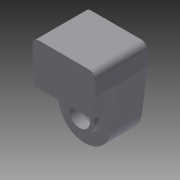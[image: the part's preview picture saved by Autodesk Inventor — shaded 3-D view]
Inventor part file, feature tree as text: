
AUTODESK INVENTOR PART (.ipt)
format: ipt  version: 2013 (Build 170138000, 138)  size: 182,272 bytes
history: native  units: in
note: dims shown in document units (in); Inventor stores cm internally (conversion verified against a paired STEP export)
features: extrude x7, sketch x7, projected_geometry x3, plane x1, fillet x1
ambient origin geometry x8: Origin, YZ Plane, XZ Plane, XY Plane, X Axis, Y Axis, Z Axis, Center Point
bodies: Solid1 (feature_tree)
feature tree (19):
  extrude  "Extrusion1"  Depth=0.1969in TaperAngle=0.0deg
  extrude  "Extrusion2"  Depth=0.0787in
  extrude  "Extrusion3"  Depth=0.0984in
  extrude  "Extrusion5"  Depth=0.0394in
  plane  "Work Plane1"
  extrude  "Extrusion6"  Depth=0.3937in TaperAngle=0.0deg
  sketch  "Sketch7"  dims[d14=0.0984in d15=0.0in d20=0.0197in d21=0.0in]
  fillet  "Fillet1"  Radius=0.0787in
  extrude  "Extrusion7"  Depth=0.0197in TaperAngle=0.0deg
  extrude  "Extrusion8"  Depth=0.0787in TaperAngle=0.0deg
  sketch  "Sketch1"  dims[d0=0.0787in d1=0.1969in d2=0.0in]
  sketch  "Sketch2"  dims[d3=0.15in d4=0.0787in]
  sketch  "Sketch3"  dims[d5=0.2362in d6=0.0984in]
  sketch  "Sketch5"  dims[d7=0.0394in d9=0.0394in]
  sketch  "Sketch6"  dims[d10=0.315in d11=0.3937in d12=0.0in d13=0.0787in]
  projected_geometry  "Projected Loop1"
  projected_geometry  "Projected Loop2"
  projected_geometry  "Projected Loop3"
  sketch  "Sketch8"  dims[d22=-0.3346in d23=0.0787in d24=0.0787in d25=0.0in d26=0.0in d28=0.0039in d29=0.0039in d30=0.0039in d32=0.0236in d33=0.0787in d34=0.0in d35=0.0787in d36=0.1102in d37=0.0787in d38=0.0197in d39=0.0in]
